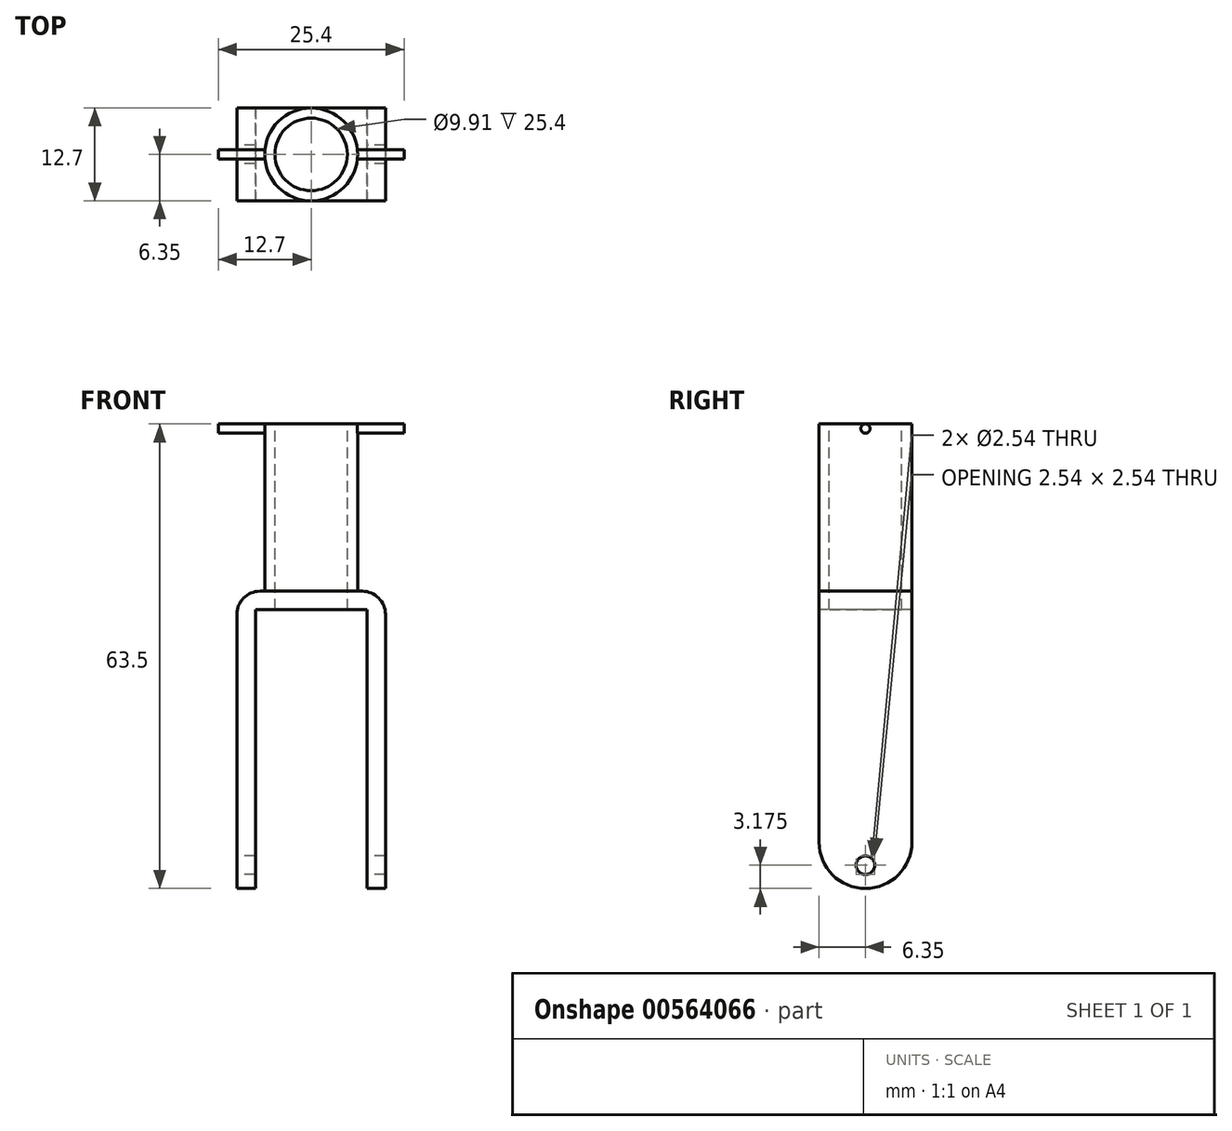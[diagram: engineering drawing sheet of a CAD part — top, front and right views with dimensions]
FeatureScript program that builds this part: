
annotation { "Feature Type Name" : "Feature", "Feature Type Description" : "" }
export const myFeature = defineFeature(function(context is Context, id is Id, definition is map)
    precondition{}
    {
        {
            var Q0;
            Q0=qCreatedBy(makeId("Top.planeOp"),FACE);
            var sketch = newSketch(context, id + "F0", { "sketchPlane" : qUnion([Q0])});
            skCircle(sketch, "E0", {"center": v(0, 0) * mm, "radius": 6.35 * mm});
            skCircle(sketch, "E1", {"center": v(0, 0) * mm, "radius": 0.64 * mm});
            skSolve(sketch);
        }
        {
            var Q0;
            Q0=makeQuery(id+"F0.imprint","IMPRINT",FACE,{"disambiguationData":[TD([[makeQuery(id+"F0.imprint","IMPRINT",EDGE,{"derivedFrom":sQuery(id+"F0.wireOp",EDGE,"E0")}),1.0]])]});
            extrude(context, id + "F1", {"entities" : qUnion([Q0]), "depth" : 63.5 * mm, "offsetDistance" : 25.4 * mm});
        }
        {
            var Q0;
            Q0=makeQuery(id+"F1.opExtrude","CAP_FACE",FACE,{"disambiguationData":[OSD([sQuery(id+"F0.wireOp",EDGE,"E0"),sQuery(id+"F0.wireOp",EDGE,"E1")])],"isStart":false});
            var sketch = newSketch(context, id + "F2", { "sketchPlane" : qUnion([Q0])});
            skLineSegment(sketch, "E2.bottom", {"start": v(12.7, -0.63) * mm, "end": v(-12.7, -0.64) * mm});
            skLineSegment(sketch, "E2.top", {"start": v(12.7, 0.64) * mm, "end": v(-12.7, 0.63) * mm});
            skLineSegment(sketch, "E2.left", {"start": v(12.7, -0.63) * mm, "end": v(12.7, 0.64) * mm});
            skLineSegment(sketch, "E2.right", {"start": v(-12.7, -0.64) * mm, "end": v(-12.7, 0.63) * mm});
            skSolve(sketch);
        }
        {
            var Q0;
            {var subQ0=sQuery(id+"F2.wireOp",EDGE,"E2.left");Q0=makeQuery(id+"F2.imprint","IMPRINT",FACE,{"disambiguationData":[TD([[makeQuery(id+"F2.imprint","IMPRINT",EDGE,{"derivedFrom":subQ0}),1.0]])]});}
            var Q1;
            {var subQ0=sQuery(id+"F2.wireOp",EDGE,"E2.right");Q1=makeQuery(id+"F2.imprint","IMPRINT",FACE,{"disambiguationData":[TD([[makeQuery(id+"F2.imprint","IMPRINT",EDGE,{"derivedFrom":subQ0}),-1.0]])]});}
            extrude(context, id + "F3", {"entities" : qUnion([Q0, Q1]), "operationType" : NewBodyOperationType.ADD, "oppositeDirection" : true, "depth" : 1.27 * mm, "offsetDistance" : 25.4 * mm});
        }
        {
            var Q0;
            {var subQ0=sQuery(id+"F2.wireOp",EDGE,"E2.top");Q0=makeQuery(id+"F3.opExtrude","CAP_EDGE",EDGE,{"disambiguationData":[OSD([subQ0]),TDD([makeQuery(id+"F2.imprint","IMPRINT",EDGE,{"disambiguationData":[TD([[makeQuery(id+"F2.imprint","INTERSECT",VERTEX,{"derivedFrom":[subQ0,sQuery(id+"F2.wireOp",EDGE,"E2.left")]}),-1.0]])],"derivedFrom":subQ0})])],"isStart":true});}
            var Q1;
            {var subQ0=sQuery(id+"F2.wireOp",EDGE,"E2.bottom");Q1=makeQuery(id+"F3.opExtrude","CAP_EDGE",EDGE,{"disambiguationData":[OSD([subQ0]),TDD([makeQuery(id+"F2.imprint","IMPRINT",EDGE,{"disambiguationData":[TD([[makeQuery(id+"F2.imprint","INTERSECT",VERTEX,{"derivedFrom":[subQ0,sQuery(id+"F2.wireOp",EDGE,"E2.left")]}),-1.0]])],"derivedFrom":subQ0})])],"isStart":true});}
            var Q2;
            {var subQ0=sQuery(id+"F2.wireOp",EDGE,"E2.top");Q2=makeQuery(id+"F3.opExtrude","CAP_EDGE",EDGE,{"disambiguationData":[OSD([subQ0]),TDD([makeQuery(id+"F2.imprint","IMPRINT",EDGE,{"disambiguationData":[TD([[makeQuery(id+"F2.imprint","INTERSECT",VERTEX,{"derivedFrom":[subQ0,sQuery(id+"F2.wireOp",EDGE,"E2.right")]}),1.0]])],"derivedFrom":subQ0})])],"isStart":true});}
            var Q3;
            {var subQ0=sQuery(id+"F2.wireOp",EDGE,"E2.bottom");Q3=makeQuery(id+"F3.opExtrude","CAP_EDGE",EDGE,{"disambiguationData":[OSD([subQ0]),TDD([makeQuery(id+"F2.imprint","IMPRINT",EDGE,{"disambiguationData":[TD([[makeQuery(id+"F2.imprint","INTERSECT",VERTEX,{"derivedFrom":[subQ0,sQuery(id+"F2.wireOp",EDGE,"E2.right")]}),1.0]])],"derivedFrom":subQ0})])],"isStart":true});}
            var Q4;
            {var subQ0=sQuery(id+"F2.wireOp",EDGE,"E2.top");Q4=makeQuery(id+"F3.opExtrude","CAP_EDGE",EDGE,{"disambiguationData":[OSD([subQ0]),TDD([makeQuery(id+"F2.imprint","IMPRINT",EDGE,{"disambiguationData":[TD([[makeQuery(id+"F2.imprint","INTERSECT",VERTEX,{"derivedFrom":[subQ0,sQuery(id+"F2.wireOp",EDGE,"E2.left")]}),-1.0]])],"derivedFrom":subQ0})])],"isStart":false});}
            var Q5;
            {var subQ0=sQuery(id+"F2.wireOp",EDGE,"E2.bottom");Q5=makeQuery(id+"F3.opExtrude","CAP_EDGE",EDGE,{"disambiguationData":[OSD([subQ0]),TDD([makeQuery(id+"F2.imprint","IMPRINT",EDGE,{"disambiguationData":[TD([[makeQuery(id+"F2.imprint","INTERSECT",VERTEX,{"derivedFrom":[subQ0,sQuery(id+"F2.wireOp",EDGE,"E2.left")]}),-1.0]])],"derivedFrom":subQ0})])],"isStart":false});}
            var Q6;
            {var subQ0=sQuery(id+"F2.wireOp",EDGE,"E2.bottom");Q6=makeQuery(id+"F3.opExtrude","CAP_EDGE",EDGE,{"disambiguationData":[OSD([subQ0]),TDD([makeQuery(id+"F2.imprint","IMPRINT",EDGE,{"disambiguationData":[TD([[makeQuery(id+"F2.imprint","INTERSECT",VERTEX,{"derivedFrom":[subQ0,sQuery(id+"F2.wireOp",EDGE,"E2.right")]}),1.0]])],"derivedFrom":subQ0})])],"isStart":false});}
            var Q7;
            {var subQ0=sQuery(id+"F2.wireOp",EDGE,"E2.top");Q7=makeQuery(id+"F3.opExtrude","CAP_EDGE",EDGE,{"disambiguationData":[OSD([subQ0]),TDD([makeQuery(id+"F2.imprint","IMPRINT",EDGE,{"disambiguationData":[TD([[makeQuery(id+"F2.imprint","INTERSECT",VERTEX,{"derivedFrom":[subQ0,sQuery(id+"F2.wireOp",EDGE,"E2.right")]}),1.0]])],"derivedFrom":subQ0})])],"isStart":false});}
            fillet(context, id + "F4", {"entities" : qUnion([Q0, Q1, Q2, Q3, Q4, Q5, Q6, Q7]), "radius" : 0.64 * mm, "tangentPropagation" : true, "allowEdgeOverflow" : false});
        }
        {
            var Q0;
            Q0=makeQuery(id+"F1.opExtrude","CAP_FACE",FACE,{"disambiguationData":[OSD([sQuery(id+"F0.wireOp",EDGE,"E0"),sQuery(id+"F0.wireOp",EDGE,"E1")])],"isStart":true});
            var sketch = newSketch(context, id + "F5", { "sketchPlane" : qUnion([Q0])});
            skLineSegment(sketch, "E3.bottom", {"start": v(10.16, 6.35) * mm, "end": v(-10.16, 6.35) * mm});
            skLineSegment(sketch, "E3.top", {"start": v(10.16, -6.35) * mm, "end": v(-10.16, -6.35) * mm});
            skLineSegment(sketch, "E3.left", {"start": v(10.16, 6.35) * mm, "end": v(10.16, -6.35) * mm});
            skLineSegment(sketch, "E3.right", {"start": v(-10.16, 6.35) * mm, "end": v(-10.16, -6.35) * mm});
            skSolve(sketch);
        }
        {
            var Q0;
            {var subQ0=sQuery(id+"F5.wireOp",EDGE,"E3.right");Q0=makeQuery(id+"F5.imprint","IMPRINT",FACE,{"disambiguationData":[TD([[makeQuery(id+"F5.imprint","IMPRINT",EDGE,{"derivedFrom":subQ0}),1.0]])]});}
            var Q1;
            {var subQ0=sQuery(id+"F5.wireOp",EDGE,"E3.left");Q1=makeQuery(id+"F5.imprint","IMPRINT",FACE,{"disambiguationData":[TD([[makeQuery(id+"F5.imprint","IMPRINT",EDGE,{"derivedFrom":subQ0}),-1.0]])]});}
            var Q2;
            Q2=makeQuery(id+"F5.imprint","IMPRINT",FACE,{"disambiguationData":[TD([[makeQuery(id+"F5.imprint","IMPRINT",EDGE,{"derivedFrom":makeQuery(id+"F1.opExtrude","CAP_EDGE",EDGE,{"disambiguationData":[OSD([sQuery(id+"F0.wireOp",EDGE,"E1")])],"isStart":true})}),1.0]])]});
            extrude(context, id + "F6", {"entities" : qUnion([Q0, Q1, Q2]), "operationType" : NewBodyOperationType.ADD, "oppositeDirection" : true, "depth" : 40.64 * mm, "offsetDistance" : 25.4 * mm});
        }
        {
            var Q0;
            Q0=makeQuery(id+"F6.opExtrude","SWEPT_FACE",FACE,{"disambiguationData":[OSD([sQuery(id+"F5.wireOp",EDGE,"E3.right")])]});
            var sketch = newSketch(context, id + "F7", { "sketchPlane" : qUnion([Q0])});
            skCircle(sketch, "E4", {"center": v(0, 3.18) * mm, "radius": 1.27 * mm});
            skSolve(sketch);
        }
        {
            var Q0;
            Q0=makeQuery(id+"F7.imprint","IMPRINT",FACE,{"disambiguationData":[TD([[makeQuery(id+"F7.imprint","IMPRINT",EDGE,{"derivedFrom":sQuery(id+"F7.wireOp",EDGE,"E4")}),1.0]])]});
            extrude(context, id + "F8", {"entities" : qUnion([Q0]), "operationType" : NewBodyOperationType.REMOVE, "oppositeDirection" : true, "depth" : 25.4 * mm, "offsetDistance" : 25.4 * mm});
        }
        {
            var Q0;
            Q0=makeQuery(id+"F6.opExtrude","SWEPT_FACE",FACE,{"disambiguationData":[OSD([sQuery(id+"F5.wireOp",EDGE,"E3.bottom")])]});
            var sketch = newSketch(context, id + "F9", { "sketchPlane" : qUnion([Q0])});
            skLineSegment(sketch, "E5.bottom", {"start": v(7.62, 0) * mm, "end": v(-7.62, 0) * mm});
            skLineSegment(sketch, "E5.top", {"start": v(7.62, 38.1) * mm, "end": v(-7.62, 38.1) * mm});
            skLineSegment(sketch, "E5.left", {"start": v(7.62, 0) * mm, "end": v(7.62, 38.1) * mm});
            skLineSegment(sketch, "E5.right", {"start": v(-7.62, 0) * mm, "end": v(-7.62, 38.1) * mm});
            skSolve(sketch);
        }
        {
            var Q0;
            Q0=makeQuery(id+"F9.imprint","IMPRINT",FACE,{"disambiguationData":[TD([[makeQuery(id+"F9.imprint","IMPRINT",EDGE,{"derivedFrom":sQuery(id+"F9.wireOp",EDGE,"E5.bottom")}),-1.0]])]});
            extrude(context, id + "F10", {"entities" : qUnion([Q0]), "operationType" : NewBodyOperationType.REMOVE, "oppositeDirection" : true, "depth" : 12.7 * mm, "offsetDistance" : 25.4 * mm});
        }
        {
            var Q0;
            {var subQ0=sQuery(id+"F2.wireOp",EDGE,"E2.top");var subQ1=sQuery(id+"F2.wireOp",EDGE,"E2.bottom");var subQ2=sQuery(id+"F0.wireOp",EDGE,"E0");Q0=makeQuery(id+"F3.boolean.opBoolean","MERGE",FACE,{"derivedFrom":[makeQuery(id+"F1.opExtrude","CAP_FACE",FACE,{"disambiguationData":[OSD([subQ2,sQuery(id+"F0.wireOp",EDGE,"E1")])],"isStart":false}),makeQuery(id+"F3.opExtrude","CAP_FACE",FACE,{"disambiguationData":[OSD([subQ2,subQ1,subQ0,sQuery(id+"F2.wireOp",EDGE,"E2.left")])],"isStart":true}),makeQuery(id+"F3.opExtrude","CAP_FACE",FACE,{"disambiguationData":[OSD([subQ2,subQ1,subQ0,sQuery(id+"F2.wireOp",EDGE,"E2.right")])],"isStart":true})]});}
            var sketch = newSketch(context, id + "F11", { "sketchPlane" : qUnion([Q0])});
            skCircle(sketch, "E6", {"center": v(0, 0) * mm, "radius": 4.95 * mm});
            skSolve(sketch);
        }
        {
            var Q0;
            Q0=makeQuery(id+"F11.imprint","IMPRINT",FACE,{"disambiguationData":[TD([[makeQuery(id+"F11.imprint","IMPRINT",EDGE,{"derivedFrom":sQuery(id+"F11.wireOp",EDGE,"E6")}),1.0]])]});
            extrude(context, id + "F12", {"entities" : qUnion([Q0]), "operationType" : NewBodyOperationType.REMOVE, "endBound" : BoundingType.UP_TO_NEXT, "oppositeDirection" : true, "depth" : 25.4 * mm, "offsetDistance" : 25.4 * mm});
        }
        {
            var Q0;
            {var subQ0=sQuery(id+"F5.wireOp",EDGE,"E3.left");var subQ1=sQuery(id+"F5.wireOp",EDGE,"E3.top");Q0=makeQuery(id+"F10.boolean.opBoolean","SPLIT",EDGE,{"disambiguationData":[TD([makeQuery(id+"F6.opExtrude","SWEPT_FACE",FACE,{"disambiguationData":[OSD([subQ0])]})])],"derivedFrom":makeQuery(id+"F6.opExtrude","CAP_EDGE",EDGE,{"disambiguationData":[OSD([subQ1])],"isStart":true})});}
            var Q1;
            {var subQ0=sQuery(id+"F5.wireOp",EDGE,"E3.left");var subQ1=sQuery(id+"F5.wireOp",EDGE,"E3.bottom");Q1=makeQuery(id+"F10.boolean.opBoolean","SPLIT",EDGE,{"disambiguationData":[TD([makeQuery(id+"F6.opExtrude","SWEPT_FACE",FACE,{"disambiguationData":[OSD([subQ0])]})])],"derivedFrom":makeQuery(id+"F6.opExtrude","CAP_EDGE",EDGE,{"disambiguationData":[OSD([subQ1])],"isStart":true})});}
            var Q2;
            {var subQ0=sQuery(id+"F5.wireOp",EDGE,"E3.right");var subQ1=sQuery(id+"F5.wireOp",EDGE,"E3.bottom");Q2=makeQuery(id+"F10.boolean.opBoolean","SPLIT",EDGE,{"disambiguationData":[TD([makeQuery(id+"F6.opExtrude","SWEPT_FACE",FACE,{"disambiguationData":[OSD([subQ0])]})])],"derivedFrom":makeQuery(id+"F6.opExtrude","CAP_EDGE",EDGE,{"disambiguationData":[OSD([subQ1])],"isStart":true})});}
            var Q3;
            {var subQ0=sQuery(id+"F5.wireOp",EDGE,"E3.right");var subQ1=sQuery(id+"F5.wireOp",EDGE,"E3.top");Q3=makeQuery(id+"F10.boolean.opBoolean","SPLIT",EDGE,{"disambiguationData":[TD([makeQuery(id+"F6.opExtrude","SWEPT_FACE",FACE,{"disambiguationData":[OSD([subQ0])]})])],"derivedFrom":makeQuery(id+"F6.opExtrude","CAP_EDGE",EDGE,{"disambiguationData":[OSD([subQ1])],"isStart":true})});}
            fillet(context, id + "F13", {"entities" : qUnion([Q0, Q1, Q2, Q3]), "radius" : 6.35 * mm, "tangentPropagation" : true, "allowEdgeOverflow" : false});
        }
        {
            var Q0;
            Q0=makeQuery(id+"F6.opExtrude","CAP_EDGE",EDGE,{"disambiguationData":[OSD([sQuery(id+"F5.wireOp",EDGE,"E3.left")])],"isStart":false});
            var Q1;
            Q1=makeQuery(id+"F6.opExtrude","CAP_EDGE",EDGE,{"disambiguationData":[OSD([sQuery(id+"F5.wireOp",EDGE,"E3.right")])],"isStart":false});
            fillet(context, id + "F14", {"entities" : qUnion([Q0, Q1]), "radius" : 3.17 * mm, "tangentPropagation" : true, "allowEdgeOverflow" : false});
        }
    });
